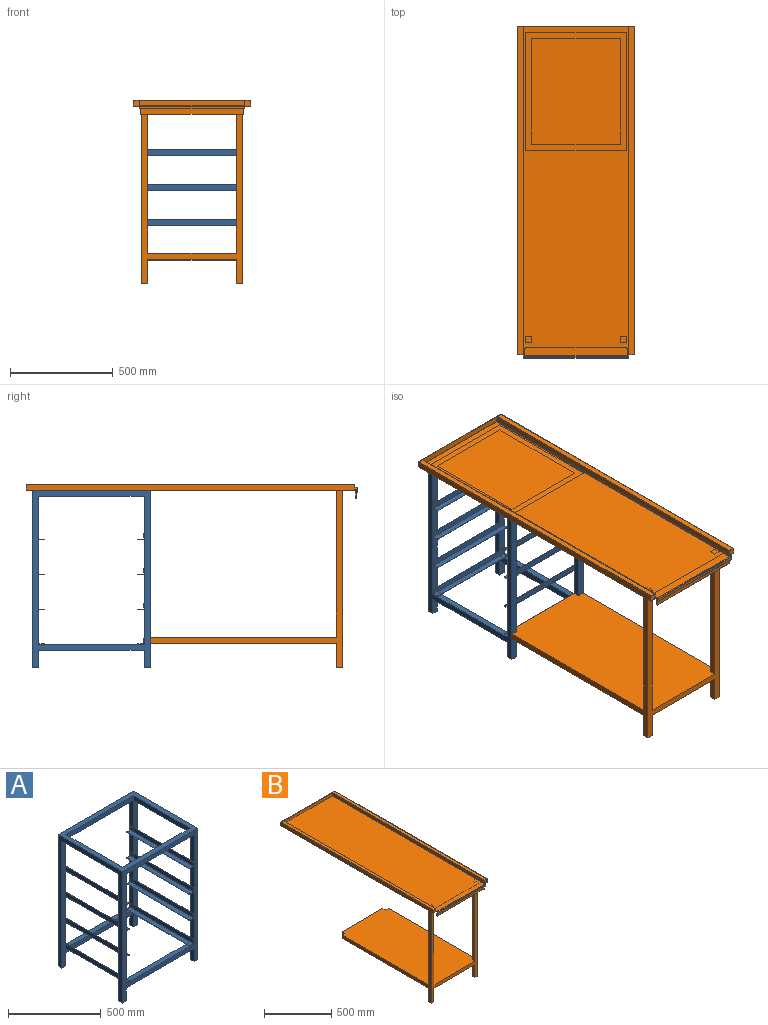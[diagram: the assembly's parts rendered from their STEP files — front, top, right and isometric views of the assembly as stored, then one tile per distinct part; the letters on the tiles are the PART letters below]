
ASSEMBLY  parts=2 mates=1
PART A: 127 faces, bbox 575x490x865 mm
  f0: plane 720x30mm, normal (-1,0,0), area 18621.5mm2, adj f3,f18,f20,f26,f82,f84,f90,f93
  f1: plane 515x30mm, normal (0,0,1), area 13960.7mm2, adj f5,f6,f8,f12,f35,f38,f39,f83
  f2: plane 720x30mm, normal (1,0,0), area 18621.5mm2, adj f3,f18,f20,f26,f34,f36,f42,f45
  f3: plane 515x30mm, normal (0,0,1), area 13960.7mm2, adj f0,f2,f18,f20,f36,f38,f40,f84
  f4: plane 515x30mm, normal (0,1,0), area 15450mm2, adj f10,f17,f28,f29
  f5: plane 835x575mm, normal (0,1,0), area 65550mm2, adj f1,f6,f7,f9,f11,f12,f13,f14
  f6: plane 720x30mm, normal (1,0,0), area 18621.5mm2, adj f1,f5,f8,f17,f34,f35,f41,f45
  f7: plane 865x490mm, normal (-1,0,0), area 64800mm2, adj f5,f8,f10,f11,f18,f20,f22,f27
  f8: plane 865x575mm, normal (0,-1,0), area 82800mm2, adj f1,f6,f7,f9,f10,f11,f12,f13
  f9: plane 85x30mm, normal (1,0,0), area 2550mm2, adj f5,f8,f11,f16
  f10: plane 575x490mm, normal (0,0,1), area 60300mm2, adj f4,f7,f8,f13,f20,f21,f28,f29
  f11: plane 30x30mm, normal (0,0,-1), area 900mm2, adj f5,f7,f8,f9
  f12: plane 720x30mm, normal (-1,0,0), area 18621.5mm2, adj f1,f5,f8,f17,f82,f83,f89,f93
  f13: plane 865x490mm, normal (1,0,0), area 64800mm2, adj f5,f8,f10,f15,f18,f20,f24,f30
  f14: plane 85x30mm, normal (-1,0,0), area 2550mm2, adj f5,f8,f15,f16
  f15: plane 30x30mm, normal (0,0,-1), area 900mm2, adj f5,f8,f13,f14
  f16: plane 515x30mm, normal (0,0,-1), area 15450mm2, adj f5,f8,f9,f14
  f17: plane 515x30mm, normal (0,0,-1), area 15450mm2, adj f4,f6,f8,f12
  f18: plane 835x575mm, normal (0,-1,0), area 65550mm2, adj f0,f2,f3,f7,f13,f19,f22,f23
  f19: plane 85x30mm, normal (1,0,0), area 2550mm2, adj f18,f20,f22,f25
  f20: plane 865x575mm, normal (0,1,0), area 82800mm2, adj f0,f2,f3,f7,f10,f13,f19,f22
  f21: plane 515x30mm, normal (0,-1,0), area 15450mm2, adj f10,f26,f28,f29
  f22: plane 30x30mm, normal (0,0,-1), area 900mm2, adj f7,f18,f19,f20
  f23: plane 85x30mm, normal (-1,0,0), area 2550mm2, adj f18,f20,f24,f25
  f24: plane 30x30mm, normal (0,0,-1), area 900mm2, adj f13,f18,f20,f23
  f25: plane 515x30mm, normal (0,0,-1), area 15450mm2, adj f18,f19,f20,f23
  f26: plane 515x30mm, normal (0,0,-1), area 15450mm2, adj f0,f2,f20,f21
  f27: plane 430x30mm, normal (0,0,-1), area 12900mm2, adj f5,f7,f18,f28
  f28: plane 430x30mm, normal (1,0,0), area 12900mm2, adj f4,f10,f21,f27
  f29: plane 430x30mm, normal (-1,0,0), area 12900mm2, adj f4,f10,f21,f30
  f30: plane 430x30mm, normal (0,0,-1), area 12900mm2, adj f5,f13,f18,f29
  f31: plane 430x30mm, normal (0,0,-1), area 12900mm2, adj f5,f18,f32,f38
  f32: plane 430x30mm, normal (-1,0,0), area 12900mm2, adj f5,f18,f31,f34
  f33: plane 480x28.5mm, normal (1,0,0), area 13669.3mm2, adj f34,f35,f36,f37,f41,f42
  f34: plane 470x1.5mm, normal (0,0,1), area 705mm2, adj f2,f6,f32,f33,f41,f42
  f35: plane 25x25mm, normal (0,-1,0), area 72.8mm2, adj f1,f6,f33,f37,f39,f41
  f36: plane 25x25mm, normal (0,1,0), area 72.8mm2, adj f2,f3,f33,f37,f40,f42
  f37: plane 480x28.5mm, normal (0,0,1), area 13669.3mm2, adj f33,f35,f36,f38,f39,f40
  f38: plane 470x1.5mm, normal (1,0,0), area 705mm2, adj f1,f3,f31,f37,f39,f40
  f39: cylinder r=5mm len=5mm, axis (0,0,1), area 11.8mm2, adj f1,f35,f37,f38
  f40: cylinder r=5mm len=5mm, axis (0,0,-1), area 11.8mm2, adj f3,f36,f37,f38
  f41: cylinder r=5mm len=5mm, axis (-1,0,0), area 11.8mm2, adj f6,f33,f34,f35
  f42: cylinder r=5mm len=5mm, axis (1,0,0), area 11.8mm2, adj f2,f33,f34,f36
  f43: plane 430x30mm, normal (-1,0,0), area 12900mm2, adj f5,f18,f45,f47
  f44: plane 480x28.5mm, normal (1,0,0), area 13669.3mm2, adj f45,f46,f48,f49,f53,f54
  f45: plane 470x1.5mm, normal (0,0,1), area 705mm2, adj f2,f6,f43,f44,f53,f54
  f46: plane 25x25mm, normal (0,-1,0), area 72.8mm2, adj f6,f44,f47,f49,f52,f54
  f47: plane 480x30mm, normal (0,0,-1), area 14389.3mm2, adj f2,f6,f43,f46,f48,f50,f51,f52
  f48: plane 25x25mm, normal (0,1,0), area 72.8mm2, adj f2,f44,f47,f49,f51,f53
  f49: plane 480x28.5mm, normal (0,0,1), area 13669.3mm2, adj f44,f46,f48,f50,f51,f52
  f50: plane 470x1.5mm, normal (1,0,0), area 705mm2, adj f47,f49,f51,f52
  f51: cylinder r=5mm len=5mm, axis (0,0,-1), area 11.8mm2, adj f47,f48,f49,f50
  f52: cylinder r=5mm len=5mm, axis (0,0,1), area 11.8mm2, adj f46,f47,f49,f50
  f53: cylinder r=5mm len=5mm, axis (1,0,0), area 11.8mm2, adj f2,f44,f45,f48
  f54: cylinder r=5mm len=5mm, axis (-1,0,0), area 11.8mm2, adj f6,f44,f45,f46
  f55: plane 430x30mm, normal (-1,0,0), area 12900mm2, adj f5,f18,f57,f59
  f56: plane 480x28.5mm, normal (1,0,0), area 13669.3mm2, adj f57,f58,f60,f61,f65,f66
  f57: plane 470x1.5mm, normal (0,0,1), area 705mm2, adj f2,f6,f55,f56,f65,f66
  f58: plane 25x25mm, normal (0,-1,0), area 72.8mm2, adj f6,f56,f59,f61,f64,f65
  f59: plane 480x30mm, normal (0,0,-1), area 14389.3mm2, adj f2,f6,f55,f58,f60,f62,f63,f64
  f60: plane 25x25mm, normal (0,1,0), area 72.8mm2, adj f2,f56,f59,f61,f63,f66
  f61: plane 480x28.5mm, normal (0,0,1), area 13669.3mm2, adj f56,f58,f60,f62,f63,f64
  f62: plane 470x1.5mm, normal (1,0,0), area 705mm2, adj f59,f61,f63,f64
  f63: cylinder r=5mm len=5mm, axis (0,0,-1), area 11.8mm2, adj f59,f60,f61,f62
  f64: cylinder r=5mm len=5mm, axis (0,0,1), area 11.8mm2, adj f58,f59,f61,f62
  f65: cylinder r=5mm len=5mm, axis (-1,0,0), area 11.8mm2, adj f6,f56,f57,f58
  f66: cylinder r=5mm len=5mm, axis (1,0,0), area 11.8mm2, adj f2,f56,f57,f60
  f67: plane 430x30mm, normal (-1,0,0), area 12900mm2, adj f5,f18,f69,f71
  f68: plane 480x28.5mm, normal (1,0,0), area 13669.3mm2, adj f69,f70,f72,f73,f77,f78
  f69: plane 470x1.5mm, normal (0,0,1), area 705mm2, adj f2,f6,f67,f68,f77,f78
  f70: plane 25x25mm, normal (0,-1,0), area 72.7mm2, adj f6,f68,f71,f73,f76,f77
  f71: plane 480x30mm, normal (0,0,-1), area 14389.3mm2, adj f2,f6,f67,f70,f72,f74,f75,f76
  f72: plane 25x25mm, normal (0,1,0), area 72.7mm2, adj f2,f68,f71,f73,f75,f78
  f73: plane 480x28.5mm, normal (0,0,1), area 13669.3mm2, adj f68,f70,f72,f74,f75,f76
  f74: plane 470x1.5mm, normal (1,0,0), area 705mm2, adj f71,f73,f75,f76
  f75: cylinder r=5mm len=5mm, axis (0,0,-1), area 11.8mm2, adj f71,f72,f73,f74
  f76: cylinder r=5mm len=5mm, axis (0,0,1), area 11.8mm2, adj f70,f71,f73,f74
  f77: cylinder r=5mm len=5mm, axis (-1,0,0), area 11.8mm2, adj f6,f68,f69,f70
  f78: cylinder r=5mm len=5mm, axis (1,0,0), area 11.8mm2, adj f2,f68,f69,f72
  f79: plane 430x30mm, normal (0,0,-1), area 12900mm2, adj f5,f18,f80,f86
  f80: plane 430x30mm, normal (1,0,0), area 12900mm2, adj f5,f18,f79,f82
  f81: plane 480x28.5mm, normal (-1,0,0), area 13669.3mm2, adj f82,f83,f84,f85,f89,f90
  f82: plane 470x1.5mm, normal (0,0,1), area 705mm2, adj f0,f12,f80,f81,f89,f90
  f83: plane 25x25mm, normal (0,-1,0), area 72.8mm2, adj f1,f12,f81,f85,f87,f89
  f84: plane 25x25mm, normal (0,1,0), area 72.8mm2, adj f0,f3,f81,f85,f88,f90
  f85: plane 480x28.5mm, normal (0,0,1), area 13669.3mm2, adj f81,f83,f84,f86,f87,f88
  f86: plane 470x1.5mm, normal (-1,0,0), area 705mm2, adj f1,f3,f79,f85,f87,f88
  f87: cylinder r=5mm len=5mm, axis (0,0,1), area 11.8mm2, adj f1,f83,f85,f86
  f88: cylinder r=5mm len=5mm, axis (0,0,-1), area 11.8mm2, adj f3,f84,f85,f86
  f89: cylinder r=5mm len=5mm, axis (1,0,0), area 11.8mm2, adj f12,f81,f82,f83
  f90: cylinder r=5mm len=5mm, axis (-1,0,0), area 11.8mm2, adj f0,f81,f82,f84
  f91: plane 430x30mm, normal (1,0,0), area 12900mm2, adj f5,f18,f93,f95
  f92: plane 480x28.5mm, normal (-1,0,0), area 13669.3mm2, adj f93,f94,f96,f97,f101,f102
  f93: plane 470x1.5mm, normal (0,0,1), area 705mm2, adj f0,f12,f91,f92,f101,f102
  f94: plane 25x25mm, normal (0,-1,0), area 72.8mm2, adj f12,f92,f95,f97,f100,f102
  f95: plane 480x30mm, normal (0,0,-1), area 14389.3mm2, adj f0,f12,f91,f94,f96,f98,f99,f100
  f96: plane 25x25mm, normal (0,1,0), area 72.8mm2, adj f0,f92,f95,f97,f99,f101
  f97: plane 480x28.5mm, normal (0,0,1), area 13669.3mm2, adj f92,f94,f96,f98,f99,f100
  f98: plane 470x1.5mm, normal (-1,0,0), area 705mm2, adj f95,f97,f99,f100
  f99: cylinder r=5mm len=5mm, axis (0,0,-1), area 11.8mm2, adj f95,f96,f97,f98
  f100: cylinder r=5mm len=5mm, axis (0,0,1), area 11.8mm2, adj f94,f95,f97,f98
  f101: cylinder r=5mm len=5mm, axis (-1,0,0), area 11.8mm2, adj f0,f92,f93,f96
  f102: cylinder r=5mm len=5mm, axis (1,0,0), area 11.8mm2, adj f12,f92,f93,f94
  f103: plane 430x30mm, normal (1,0,0), area 12900mm2, adj f5,f18,f105,f107
  f104: plane 480x28.5mm, normal (-1,0,0), area 13669.3mm2, adj f105,f106,f108,f109,f113,f114
  f105: plane 470x1.5mm, normal (0,0,1), area 705mm2, adj f0,f12,f103,f104,f113,f114
  f106: plane 25x25mm, normal (0,-1,0), area 72.8mm2, adj f12,f104,f107,f109,f112,f113
  f107: plane 480x30mm, normal (0,0,-1), area 14389.3mm2, adj f0,f12,f103,f106,f108,f110,f111,f112
  f108: plane 25x25mm, normal (0,1,0), area 72.8mm2, adj f0,f104,f107,f109,f111,f114
  f109: plane 480x28.5mm, normal (0,0,1), area 13669.3mm2, adj f104,f106,f108,f110,f111,f112
  f110: plane 470x1.5mm, normal (-1,0,0), area 705mm2, adj f107,f109,f111,f112
  f111: cylinder r=5mm len=5mm, axis (0,0,-1), area 11.8mm2, adj f107,f108,f109,f110
  f112: cylinder r=5mm len=5mm, axis (0,0,1), area 11.8mm2, adj f106,f107,f109,f110
  f113: cylinder r=5mm len=5mm, axis (1,0,0), area 11.8mm2, adj f12,f104,f105,f106
  f114: cylinder r=5mm len=5mm, axis (-1,0,0), area 11.8mm2, adj f0,f104,f105,f108
  f115: plane 430x30mm, normal (1,0,0), area 12900mm2, adj f5,f18,f117,f119
  f116: plane 480x28.5mm, normal (-1,0,0), area 13669.3mm2, adj f117,f118,f120,f121,f125,f126
  f117: plane 470x1.5mm, normal (0,0,1), area 705mm2, adj f0,f12,f115,f116,f125,f126
  f118: plane 25x25mm, normal (0,-1,0), area 72.7mm2, adj f12,f116,f119,f121,f124,f125
  f119: plane 480x30mm, normal (0,0,-1), area 14389.3mm2, adj f0,f12,f115,f118,f120,f122,f123,f124
  f120: plane 25x25mm, normal (0,1,0), area 72.7mm2, adj f0,f116,f119,f121,f123,f126
  f121: plane 480x28.5mm, normal (0,0,1), area 13669.3mm2, adj f116,f118,f120,f122,f123,f124
  f122: plane 470x1.5mm, normal (-1,0,0), area 705mm2, adj f119,f121,f123,f124
  f123: cylinder r=5mm len=5mm, axis (0,0,-1), area 11.8mm2, adj f119,f120,f121,f122
  f124: cylinder r=5mm len=5mm, axis (0,0,1), area 11.8mm2, adj f118,f119,f121,f122
  f125: cylinder r=5mm len=5mm, axis (1,0,0), area 11.8mm2, adj f12,f116,f117,f118
  f126: cylinder r=5mm len=5mm, axis (-1,0,0), area 11.8mm2, adj f0,f116,f117,f120
PART B: 74 faces, bbox 570x1616.5x895.5 mm
  f0: plane 30x30mm, normal (0,1,0), area 900mm2, adj f66,f68,f69,f72
  f1: plane 715.5x30mm, normal (0,1,0), area 21465mm2, adj f2,f5,f59,f68
  f2: plane 715.5x30mm, normal (1,0,0), area 21465mm2, adj f1,f5,f62,f68
  f3: plane 715.5x30mm, normal (-1,0,0), area 21465mm2, adj f4,f5,f62,f68
  f4: plane 715.5x30mm, normal (0,1,0), area 21465mm2, adj f3,f5,f66,f68
  f5: plane 1615x570mm, normal (0,0,-1), area 802000.2mm2, adj f1,f2,f3,f4,f9,f10,f11,f14
  f6: plane 500x38.5mm, normal (0,0,-1), area 19239.3mm2, adj f49,f50,f51,f53,f54,f55
  f7: plane 13.5x12mm, normal (-1,0,0), area 162mm2, adj f9,f17,f39,f40
  f8: plane 1598.5x25.5mm, normal (-1,0,0), area 40761.8mm2, adj f10,f31,f35,f48
  f9: cylinder r=3mm len=13.5mm, axis (0,1,0), area 63.6mm2, adj f5,f7,f17,f40
  f10: cylinder r=3mm len=1598.5mm, axis (0,1,0), area 7532.8mm2, adj f5,f8,f35,f48
  f11: plane 1598.5x28.5mm, normal (-1,0,0), area 45557.3mm2, adj f5,f13,f34,f47
  f12: plane 13.5x12mm, normal (1,0,0), area 162mm2, adj f14,f15,f16,f38
  f13: plane 1598.5x27mm, normal (0,0,-1), area 43159.5mm2, adj f11,f33,f34,f47
  f14: cylinder r=3mm len=13.5mm, axis (0,1,0), area 63.6mm2, adj f5,f12,f15,f16
  f15: plane 15x3mm, normal (0,-1,0), area 23.3mm2, adj f12,f14,f21,f22,f38,f41
  f16: plane 31.5x30mm, normal (0,-1,0), area 878.5mm2, adj f5,f12,f14,f18,f19,f20,f21,f27
  f17: plane 31.5x30mm, normal (0,-1,0), area 878.5mm2, adj f5,f7,f9,f25,f26,f27,f28,f29
  f18: plane 1601.5x28.5mm, normal (1,0,0), area 45642.8mm2, adj f5,f16,f19,f36
  f19: cylinder r=1.5mm len=1601.5mm, axis (0,1,0), area 3773.4mm2, adj f16,f18,f27,f36
  f20: cylinder r=1.5mm len=1600mm, axis (0,1,0), area 3769.9mm2, adj f16,f21,f27,f37
  f21: plane 1613.5x25.5mm, normal (-1,0,0), area 40962mm2, adj f15,f16,f20,f22,f37,f38
  f22: cylinder r=1.5mm len=1613.5mm, axis (0,1,0), area 3801.7mm2, adj f15,f21,f23,f37
  f23: plane 1613.5x507mm, normal (0,0,1), area 818044.5mm2, adj f22,f24,f37,f42
  f24: cylinder r=1.5mm len=1613.5mm, axis (0,1,0), area 3801.7mm2, adj f23,f25,f37,f40
  f25: plane 1613.5x25.5mm, normal (1,0,0), area 40962mm2, adj f17,f24,f26,f37,f39,f40
  f26: cylinder r=1.5mm len=1600mm, axis (0,1,0), area 3769.9mm2, adj f17,f25,f27,f37
  f27: plane 1601.5x567mm, normal (0,0,1), area 87250.5mm2, adj f16,f17,f19,f20,f26,f28,f36,f37
  f28: cylinder r=1.5mm len=1601.5mm, axis (0,1,0), area 3773.4mm2, adj f17,f27,f29,f36
  f29: plane 1601.5x28.5mm, normal (-1,0,0), area 45642.8mm2, adj f5,f17,f28,f36
  f30: plane 1598.5x28.5mm, normal (1,0,0), area 45557.3mm2, adj f5,f31,f35,f48
  f31: plane 1598.5x27mm, normal (0,0,-1), area 43159.5mm2, adj f8,f30,f35,f48
  f32: cylinder r=3mm len=1598.5mm, axis (0,1,0), area 7532.8mm2, adj f5,f33,f34,f47
  f33: plane 1598.5x25.5mm, normal (1,0,0), area 40761.8mm2, adj f13,f32,f34,f47
  f34: plane 30x28.5mm, normal (0,-1,0), area 771.4mm2, adj f5,f11,f13,f32,f33
  f35: plane 30x28.5mm, normal (0,-1,0), area 771.4mm2, adj f5,f8,f10,f30,f31
  f36: plane 570x30mm, normal (0,1,0), area 17099mm2, adj f5,f18,f19,f27,f28,f29
  f37: plane 513x28.5mm, normal (0,-1,0), area 14535mm2, adj f20,f21,f22,f23,f24,f25,f26,f27
  f38: plane 13.5x1.5mm, normal (0,0,1), area 20.2mm2, adj f12,f15,f16,f21
  f39: plane 13.5x1.5mm, normal (0,0,1), area 20.2mm2, adj f7,f17,f25,f40
  f40: plane 15x3mm, normal (0,-1,0), area 23.3mm2, adj f7,f9,f24,f25,f39,f43
  f41: plane 15x1.5mm, normal (1,0,0), area 22mm2, adj f15,f42,f44,f45,f46
  f42: cylinder r=1.5mm len=507mm, axis (-1,0,0), area 1194.6mm2, adj f23,f41,f43,f45
  f43: plane 15x1.5mm, normal (-1,0,0), area 22mm2, adj f40,f42,f44,f45,f46
  f44: plane 507x13.5mm, normal (0,1,0), area 6844.5mm2, adj f5,f41,f43,f46
  f45: plane 507x13.5mm, normal (0,-1,0), area 6844.5mm2, adj f41,f42,f43,f46
  f46: plane 507x1.5mm, normal (0,0,-1), area 760.5mm2, adj f41,f43,f44,f45
  f47: plane 30x28.5mm, normal (0,1,0), area 771.4mm2, adj f5,f11,f13,f32,f33
  f48: plane 30x28.5mm, normal (0,1,0), area 771.4mm2, adj f5,f8,f10,f30,f31
  f49: plane 490x1.5mm, normal (0,1,0), area 735mm2, adj f5,f6,f50,f54
  f50: cylinder r=5mm len=5mm, axis (0,0,1), area 11.8mm2, adj f5,f6,f49,f51
  f51: plane 35x35mm, normal (1,0,0), area 102.7mm2, adj f5,f6,f50,f52,f55,f57
  f52: plane 500x40mm, normal (0,-1,0), area 19989.3mm2, adj f5,f51,f53,f56,f57,f58
  f53: plane 35x35mm, normal (-1,0,0), area 102.7mm2, adj f5,f6,f52,f54,f55,f58
  f54: cylinder r=5mm len=5mm, axis (0,0,1), area 11.8mm2, adj f5,f6,f49,f53
  f55: plane 500x38.5mm, normal (0,1,0), area 19239.3mm2, adj f6,f51,f53,f56,f57,f58
  f56: plane 490x1.5mm, normal (0,0,-1), area 735mm2, adj f52,f55,f57,f58
  f57: cylinder r=5mm len=5mm, axis (0,1,0), area 11.8mm2, adj f51,f52,f55,f56
  f58: cylinder r=5mm len=5mm, axis (0,-1,0), area 11.8mm2, adj f52,f53,f55,f56
  f59: plane 936.5x865.5mm, normal (-1,0,0), area 53160mm2, adj f1,f5,f60,f62,f63,f68,f69,f70
  f60: plane 120x30mm, normal (0,1,0), area 3600mm2, adj f59,f61,f63,f69
  f61: plane 120x30mm, normal (1,0,0), area 3600mm2, adj f60,f62,f63,f69
  f62: plane 865.5x490mm, normal (0,-1,0), area 64830mm2, adj f2,f3,f5,f59,f61,f63,f64,f66
  f63: plane 30x30mm, normal (0,0,-1), area 900mm2, adj f59,f60,f61,f62
  f64: plane 120x30mm, normal (-1,0,0), area 3600mm2, adj f62,f65,f67,f69
  f65: plane 120x30mm, normal (0,1,0), area 3600mm2, adj f64,f66,f67,f69
  f66: plane 936.5x865.5mm, normal (1,0,0), area 53160mm2, adj f0,f4,f5,f62,f65,f67,f68,f69
  f67: plane 30x30mm, normal (0,0,-1), area 900mm2, adj f62,f64,f65,f66
  f68: plane 966.5x490mm, normal (0,0,1), area 469985mm2, adj f0,f1,f2,f3,f4,f59,f62,f66
  f69: plane 966.5x490mm, normal (0,0,-1), area 469985mm2, adj f0,f59,f60,f61,f62,f64,f65,f66
  f70: plane 30x30mm, normal (0,1,0), area 900mm2, adj f59,f68,f69,f71
  f71: plane 30x30mm, normal (-1,0,0), area 900mm2, adj f68,f69,f70,f73
  f72: plane 30x30mm, normal (1,0,0), area 900mm2, adj f0,f68,f69,f73
  f73: plane 430x30mm, normal (0,1,0), area 12900mm2, adj f68,f69,f71,f72
PLACE A rot(axis=(0,0,1),90deg) t=(-772.19,-269.48,-694.19)mm
PLACE B t=(-772.19,46.52,170.81)mm
MATE fastened A.f10 <-> B.f5  axis (0,0,1) through (-772.19,18.02,170.81)mm
